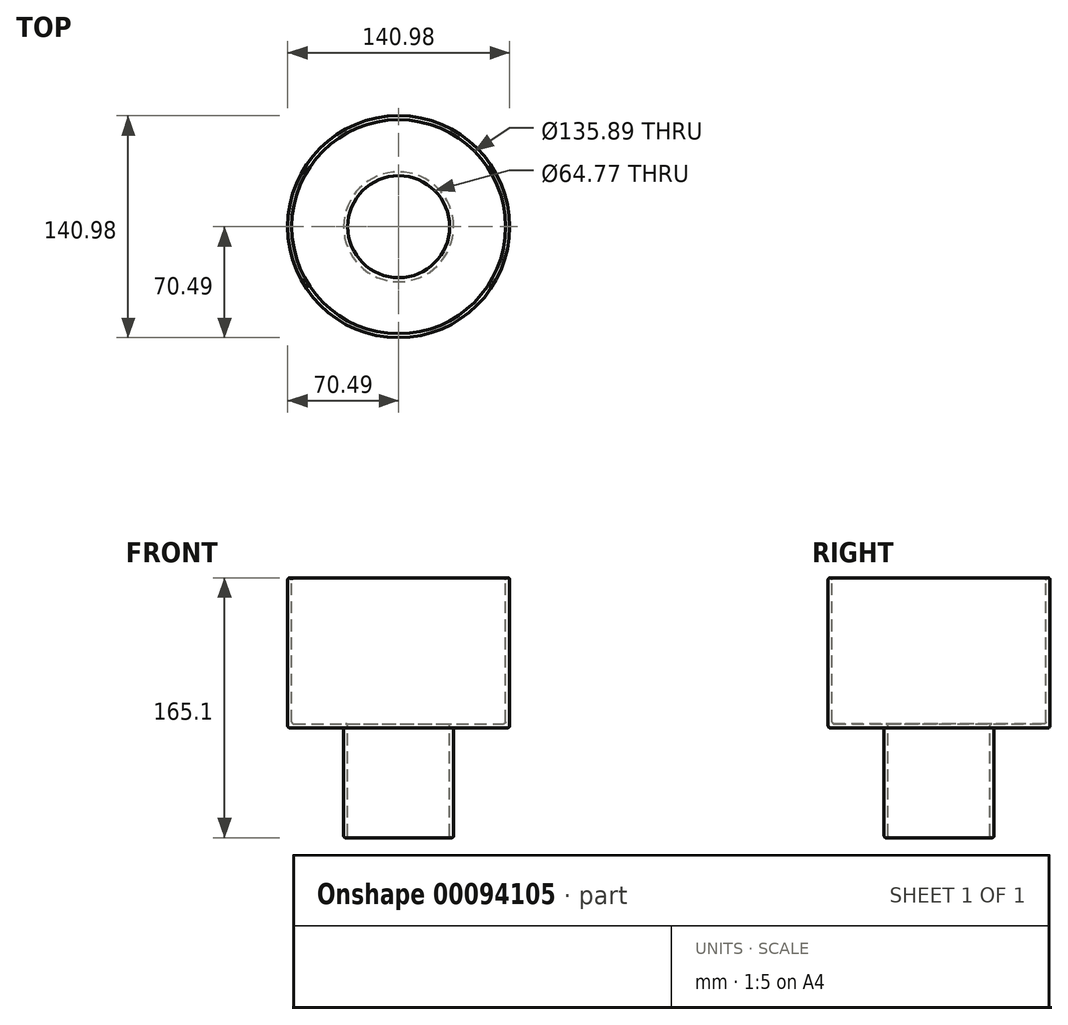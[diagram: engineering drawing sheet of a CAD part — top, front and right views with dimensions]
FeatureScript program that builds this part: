
annotation { "Feature Type Name" : "Feature", "Feature Type Description" : "" }
export const myFeature = defineFeature(function(context is Context, id is Id, definition is map)
    precondition{}
    {
        {
            var Q0;
            Q0=qCreatedBy(makeId("Front.planeOp"),FACE);
            var sketch = newSketch(context, id + "F0", { "sketchPlane" : qUnion([Q0])});
            skLineSegment(sketch, "E0.bottom", {"start": v(70.48, 95.25) * mm, "end": v(67.94, 95.25) * mm});
            skLineSegment(sketch, "E0.top", {"start": v(70.48, 0) * mm, "end": v(67.94, 0) * mm});
            skLineSegment(sketch, "E0.left", {"start": v(70.48, 95.25) * mm, "end": v(70.48, 0) * mm});
            skLineSegment(sketch, "E0.right", {"start": v(67.94, 95.25) * mm, "end": v(67.94, 0) * mm});
            skLineSegment(sketch, "E1.bottom", {"start": v(67.94, 0) * mm, "end": v(34.92, 0) * mm});
            skLineSegment(sketch, "E1.top", {"start": v(67.94, 2.54) * mm, "end": v(34.92, 2.54) * mm});
            skLineSegment(sketch, "E1.left", {"start": v(67.94, 0) * mm, "end": v(67.94, 2.54) * mm});
            skLineSegment(sketch, "E1.right", {"start": v(34.92, 0) * mm, "end": v(34.92, 2.54) * mm});
            skLineSegment(sketch, "E2.bottom", {"start": v(34.92, 2.54) * mm, "end": v(32.38, 2.54) * mm});
            skLineSegment(sketch, "E2.top", {"start": v(34.93, -69.85) * mm, "end": v(32.39, -69.85) * mm});
            skLineSegment(sketch, "E2.left", {"start": v(34.92, 2.54) * mm, "end": v(34.93, -69.85) * mm});
            skLineSegment(sketch, "E2.right", {"start": v(32.38, 2.54) * mm, "end": v(32.39, -69.85) * mm});
            skLineSegment(sketch, "E3", {"start": v(0, 66.69) * mm, "end": v(0, -74.2) * mm, "construction": true});
            skSolve(sketch);
        }
        {
            var Q0;
            Q0=makeQuery(id+"F0.imprint","IMPRINT",FACE,{"disambiguationData":[TD([[makeQuery(id+"F0.imprint","IMPRINT",EDGE,{"derivedFrom":sQuery(id+"F0.wireOp",EDGE,"E0.bottom")}),1.0]])]});
            var Q1;
            {var subQ0=sQuery(id+"F0.wireOp",EDGE,"E1.bottom");Q1=makeQuery(id+"F0.imprint","IMPRINT",FACE,{"disambiguationData":[TD([[makeQuery(id+"F0.imprint","IMPRINT",EDGE,{"derivedFrom":subQ0}),-1.0]])]});}
            var Q2;
            {var subQ3=sQuery(id+"F0.wireOp",EDGE,"E2.bottom");Q2=makeQuery(id+"F0.imprint","IMPRINT",FACE,{"disambiguationData":[TD([[makeQuery(id+"F0.imprint","IMPRINT",EDGE,{"derivedFrom":subQ3}),1.0]])]});}
            var Q3;
            Q3=sQuery(id+"F0.wireOp",EDGE,"E3");
            revolve(context, id + "F1", {"entities" : qUnion([Q0, Q1, Q2]), "axis" : qUnion([Q3]), "revolveType" : RevolveType.FULL});
        }
        {
            var Q0;
            Q0=makeQuery(id+"F1.opRevolve","SWEPT_EDGE",EDGE,{"disambiguationData":[OSD([sQuery(id+"F0.wireOp",EDGE,"E0.bottom"),sQuery(id+"F0.wireOp",EDGE,"E0.right")])]});
            var Q1;
            Q1=makeQuery(id+"F1.opRevolve","SWEPT_EDGE",EDGE,{"disambiguationData":[OSD([sQuery(id+"F0.wireOp",EDGE,"E0.bottom"),sQuery(id+"F0.wireOp",EDGE,"E0.left")])]});
            var Q2;
            Q2=makeQuery(id+"F1.opRevolve","SWEPT_EDGE",EDGE,{"disambiguationData":[OSD([sQuery(id+"F0.wireOp",EDGE,"E0.right"),sQuery(id+"F0.wireOp",EDGE,"E1.top"),sQuery(id+"F0.wireOp",EDGE,"E1.left")])]});
            var Q3;
            Q3=makeQuery(id+"F1.opRevolve","SWEPT_EDGE",EDGE,{"disambiguationData":[OSD([sQuery(id+"F0.wireOp",EDGE,"E0.top"),sQuery(id+"F0.wireOp",EDGE,"E0.left")])]});
            var Q4;
            Q4=makeQuery(id+"F1.opRevolve","SWEPT_EDGE",EDGE,{"disambiguationData":[OSD([sQuery(id+"F0.wireOp",EDGE,"E2.top"),sQuery(id+"F0.wireOp",EDGE,"E2.right")])]});
            var Q5;
            Q5=makeQuery(id+"F1.opRevolve","SWEPT_EDGE",EDGE,{"disambiguationData":[OSD([sQuery(id+"F0.wireOp",EDGE,"E2.bottom"),sQuery(id+"F0.wireOp",EDGE,"E2.right")])]});
            var Q6;
            Q6=makeQuery(id+"F1.opRevolve","SWEPT_EDGE",EDGE,{"disambiguationData":[OSD([sQuery(id+"F0.wireOp",EDGE,"E2.top"),sQuery(id+"F0.wireOp",EDGE,"E2.left")])]});
            var Q7;
            Q7=makeQuery(id+"F1.opRevolve","SWEPT_EDGE",EDGE,{"disambiguationData":[OSD([sQuery(id+"F0.wireOp",EDGE,"E1.bottom"),sQuery(id+"F0.wireOp",EDGE,"E2.left")])]});
            fillet(context, id + "F2", {"entities" : qUnion([Q0, Q1, Q2, Q3, Q4, Q5, Q6, Q7]), "radius" : 1.27 * mm, "tangentPropagation" : true, "allowEdgeOverflow" : false});
        }
    });
